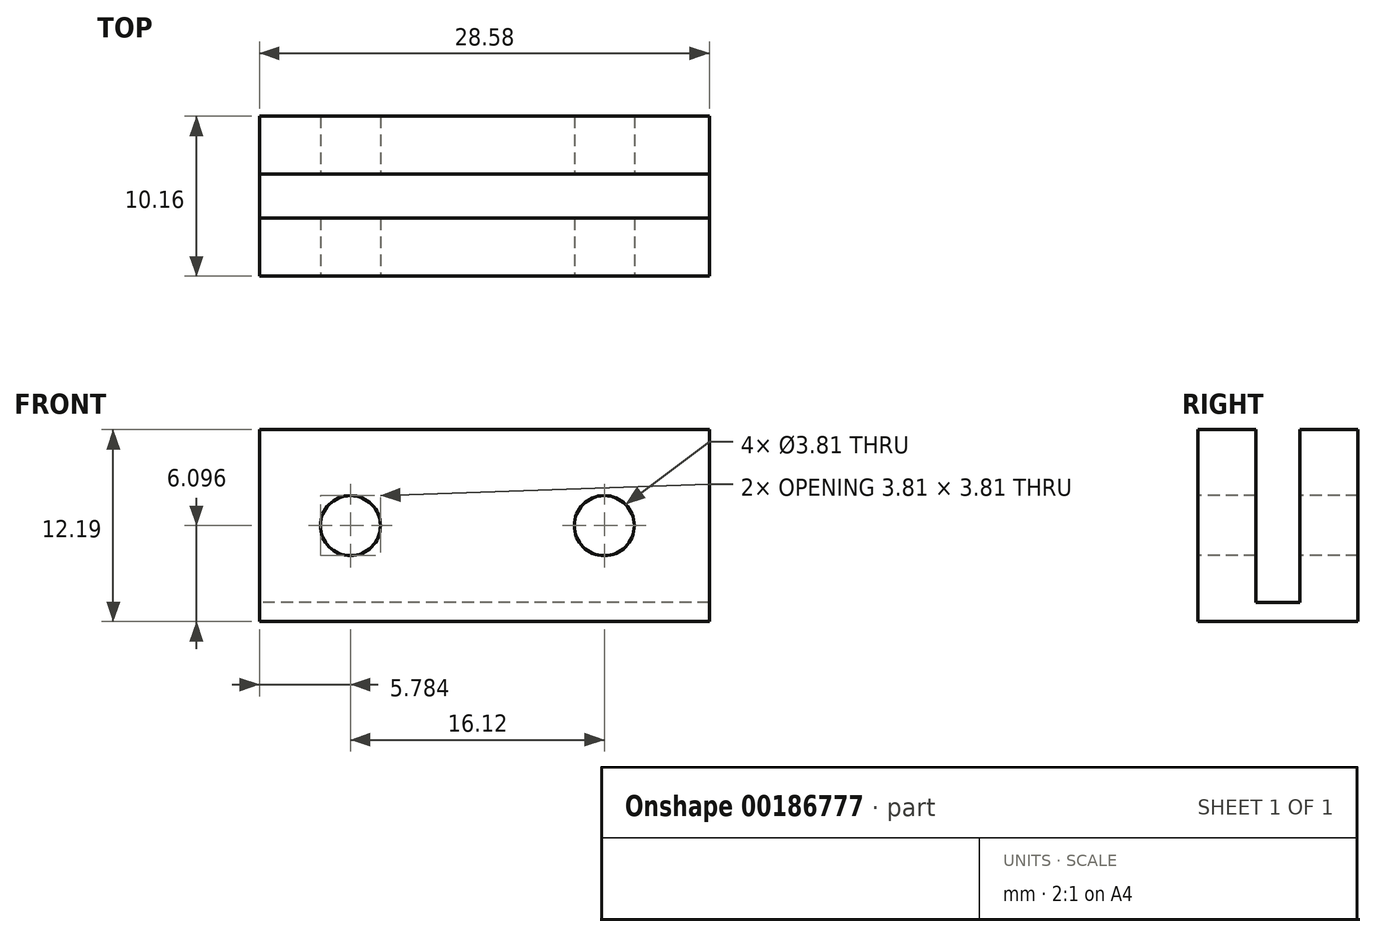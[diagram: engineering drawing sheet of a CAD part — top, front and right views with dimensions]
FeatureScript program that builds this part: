
annotation { "Feature Type Name" : "Feature", "Feature Type Description" : "" }
export const myFeature = defineFeature(function(context is Context, id is Id, definition is map)
    precondition{}
    {
        {
            var Q0;
            Q0=qCreatedBy(makeId("Top.planeOp"),FACE);
            var sketch = newSketch(context, id + "F0", { "sketchPlane" : qUnion([Q0])});
            skLineSegment(sketch, "E0.bottom", {"start": v(14.29, -5.08) * mm, "end": v(-14.29, -5.08) * mm});
            skLineSegment(sketch, "E0.top", {"start": v(14.29, 5.08) * mm, "end": v(-14.29, 5.08) * mm});
            skLineSegment(sketch, "E0.left", {"start": v(14.29, -5.08) * mm, "end": v(14.29, 5.08) * mm});
            skLineSegment(sketch, "E0.right", {"start": v(-14.29, -5.08) * mm, "end": v(-14.29, 5.08) * mm});
            skPoint(sketch, "E0.middle", {"position": v(0, 0) * mm});
            skSolve(sketch);
        }
        {
            var Q0;
            Q0 = qSketchRegion(id + "F0", true);
            extrude(context, id + "F1", {"entities" : qUnion([Q0]), "depth" : 12.2 * mm});
        }
        {
            var Q0;
            Q0=makeQuery(id+"F1.opExtrude","CAP_FACE",FACE,{"disambiguationData":[OSD([sQuery(id+"F0.wireOp",EDGE,"E0.bottom"),sQuery(id+"F0.wireOp",EDGE,"E0.top"),sQuery(id+"F0.wireOp",EDGE,"E0.left"),sQuery(id+"F0.wireOp",EDGE,"E0.right")])],"isStart":false});
            var sketch = newSketch(context, id + "F2", { "sketchPlane" : qUnion([Q0])});
            skLineSegment(sketch, "E1.bottom", {"start": v(14.29, 1.4) * mm, "end": v(-14.29, 1.4) * mm});
            skLineSegment(sketch, "E1.top", {"start": v(14.29, -1.4) * mm, "end": v(-14.29, -1.4) * mm});
            skLineSegment(sketch, "E1.left", {"start": v(14.29, 1.4) * mm, "end": v(14.29, -1.4) * mm});
            skLineSegment(sketch, "E1.right", {"start": v(-14.29, 1.4) * mm, "end": v(-14.29, -1.4) * mm});
            skPoint(sketch, "E1.middle", {"position": v(0, 0) * mm});
            skSolve(sketch);
        }
        {
            var Q0;
            Q0 = qSketchRegion(id + "F2", true);
            extrude(context, id + "F3", {"entities" : qUnion([Q0]), "operationType" : NewBodyOperationType.REMOVE, "oppositeDirection" : true, "depth" : 10.97 * mm});
        }
        {
            var Q0;
            Q0=makeQuery(id+"F1.opExtrude","SWEPT_FACE",FACE,{"disambiguationData":[OSD([sQuery(id+"F0.wireOp",EDGE,"E0.bottom")])]});
            var sketch = newSketch(context, id + "F4", { "sketchPlane" : qUnion([Q0])});
            skCircle(sketch, "E2", {"center": v(-8.5, 6.1) * mm, "radius": 1.9 * mm});
            skPoint(sketch, "E2.centerSnap0", {"position": v(-14.29, 6.1) * mm});
            skCircle(sketch, "E3", {"center": v(7.61, 6.1) * mm, "radius": 1.9 * mm});
            skPoint(sketch, "E3.centerSnap0", {"position": v(14.29, 6.1) * mm});
            skSolve(sketch);
        }
        {
            var Q0;
            Q0 = qSketchRegion(id + "F4", true);
            extrude(context, id + "F5", {"entities" : qUnion([Q0]), "operationType" : NewBodyOperationType.REMOVE, "oppositeDirection" : true, "depth" : 25.4 * mm});
        }
    });
